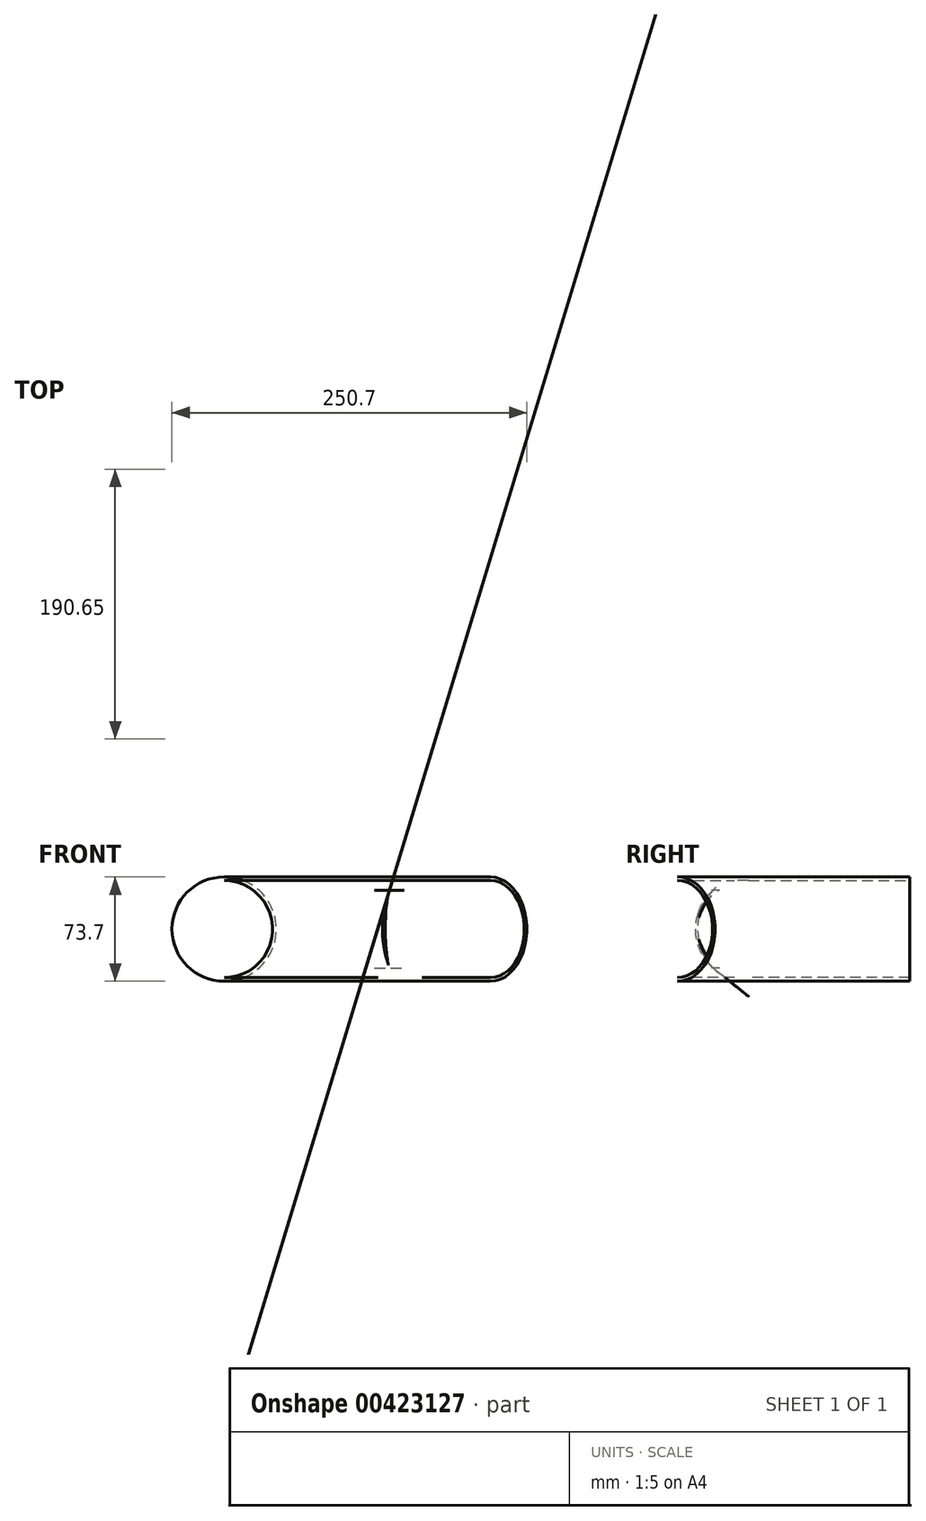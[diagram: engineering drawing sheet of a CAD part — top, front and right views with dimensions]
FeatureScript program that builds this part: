
annotation { "Feature Type Name" : "Feature", "Feature Type Description" : "" }
export const myFeature = defineFeature(function(context is Context, id is Id, definition is map)
    precondition{}
    {
        {
            var Q0;
            Q0=qCreatedBy(makeId("Front.planeOp"),FACE);
            var sketch = newSketch(context, id + "F0", { "sketchPlane" : qUnion([Q0])});
            skCircle(sketch, "E0", {"center": v(0, 0) * mm, "radius": 36.85 * mm});
            skSolve(sketch);
        }
        {
            var Q0;
            Q0=qCreatedBy(makeId("Top.planeOp"),FACE);
            var sketch = newSketch(context, id + "F1", { "sketchPlane" : qUnion([Q0])});
            skFitSpline(sketch, "E1", {"points": [v(0, 0) * mm, v(13.81, -75.21) * mm, v(58.64, -106.4) * mm, v(113.2, -114.2) * mm, v(130.75, -118.09) * mm, v(188.24, -163.89) * mm], "startDerivative": vector(17.36, -350.63) * mm, "endDerivative": vector(284.4, -248.83) * mm});
            skFitSpline(sketch, "E2", {"points": [v(188.24, -163.89) * mm, v(210.2, -185.35) * mm, v(214.8, -186.5) * mm, v(297.34, -187.66) * mm, v(316.96, -214.2) * mm, v(316.38, -214.2) * mm], "startDerivative": vector(115.88, -116.24) * mm, "endDerivative": vector(-21.13, 8.46) * mm});
            skSolve(sketch);
        }
        {
            var Q0;
            Q0=makeQuery(id+"F0.imprint","IMPRINT",FACE,{"disambiguationData":[TD([[makeQuery(id+"F0.imprint","IMPRINT",EDGE,{"derivedFrom":sQuery(id+"F0.wireOp",EDGE,"E0")}),1.0]])]});
            var Q1;
            Q1=makeQuery(id+"F67gTOUlCtCVZRG_1.imprint","IMPRINT",FACE,{"disambiguationData":[TD([[makeQuery(id+"F67gTOUlCtCVZRG_1.imprint","IMPRINT",EDGE,{"derivedFrom":sQuery(id+"F67gTOUlCtCVZRG_1.wireOp",EDGE,"GmqSCJyR-WeR5-J0xB-RfWc-xNfYuumexacV")}),1.0]])]});
            var Q2;
            Q2=sQuery(id+"F1.wireOp",EDGE,"E1");
            sweep(context, id + "F2", {"profiles" : qUnion([Q0, Q1]), "path" : qUnion([Q2])});
        }
        {
            var Q0;
            Q0=makeQuery(id+"F2.opSweep","CAP_FACE",FACE,{"disambiguationData":[OSD([sQuery(id+"F0.wireOp",EDGE,"E0"),sQuery(id+"F1.wireOp",VERTEX,"E1.end")])],"isStart":false});
            var Q1;
            Q1=makeQuery(id+"F2.opSweep","CAP_FACE",FACE,{"disambiguationData":[OSD([sQuery(id+"F0.wireOp",EDGE,"E0"),sQuery(id+"F1.wireOp",VERTEX,"E1.start")])],"isStart":true});
            shell(context, id + "F3", {"entities" : qUnion([Q0, Q1]), "thickness" : 2.54 * mm});
        }
    });
